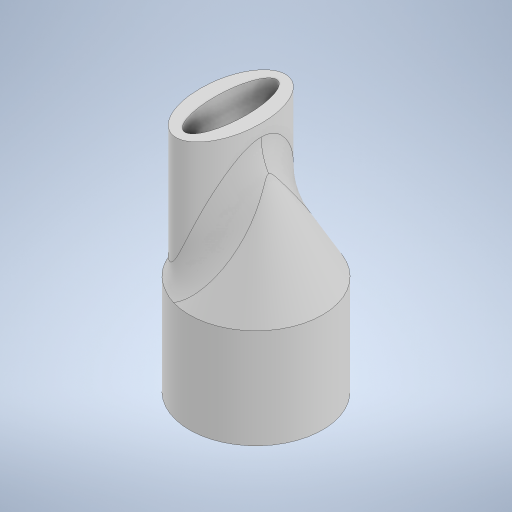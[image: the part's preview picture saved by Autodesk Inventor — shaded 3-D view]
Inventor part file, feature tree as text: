
AUTODESK INVENTOR PART (.ipt)
format: ipt  version: 2024 (Build 280153000, 153)  size: 384,512 bytes
history: native  units: mm
features: extrude x5, sketch x5, fillet x3, other x1, chamfer x1
ambient origin geometry x8: Origin, YZ Plane, XZ Plane, XY Plane, X Axis, Y Axis, Z Axis, Center Point
bodies: Body1 (feature_tree)
feature tree (15):
  other  "Твердое тело1"
  extrude  "Выдавливание1"  Depth=18.7mm
  extrude  "Выдавливание2"  Depth=14.7mm
  extrude  "Выдавливание5"  Depth=15.0mm TaperAngle=0.0deg
  extrude  "Выдавливание6"  Depth=18.0mm TaperAngle=0.0deg
  chamfer  "Фаска2"  Distance=18.0mm
  fillet  "Сопряжение1"  Radius=14.0mm
  extrude  "Выдавливание7"  Depth=8.5mm
  fillet  "Сопряжение2"  Radius=8.0mm
  fillet  "Сопряжение3"  [1 undecoded]
  sketch  "Эскиз1"
  sketch  "Эскиз2"
  sketch  "Эскиз5"
  sketch  "Эскиз6"
  sketch  "Эскиз7"
note: 1 required parameter value undecoded (feature->parameter linkage not recoverable at this tier; creation-order binding heuristic only, values carry confidence <= 0.55)
